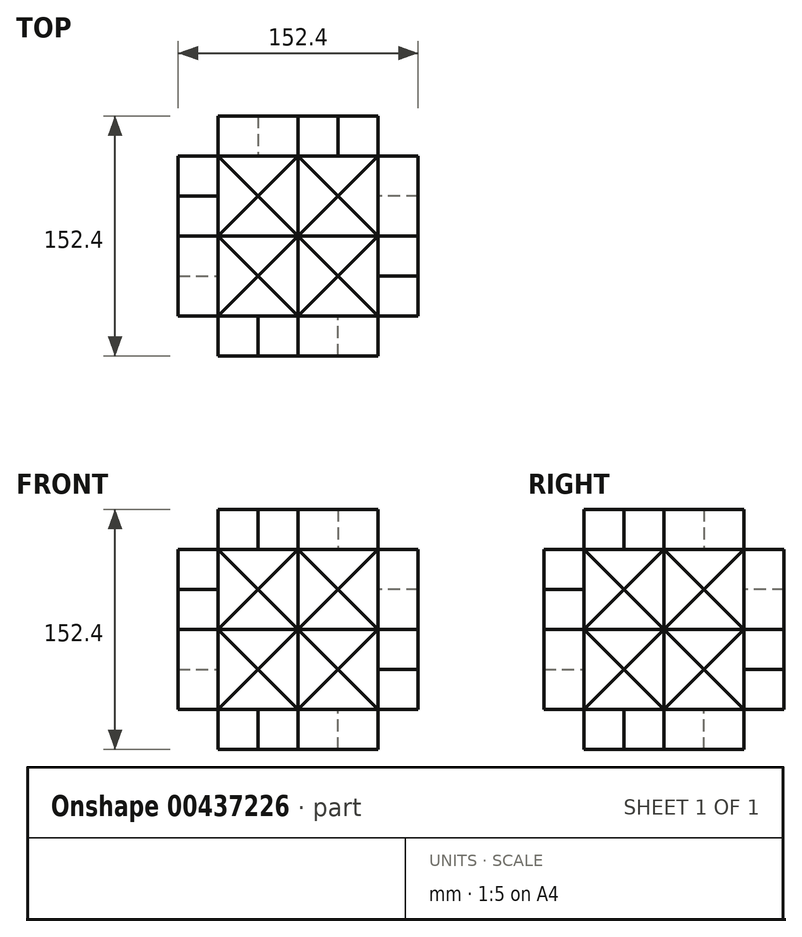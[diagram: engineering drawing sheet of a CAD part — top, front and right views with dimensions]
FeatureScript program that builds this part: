
annotation { "Feature Type Name" : "Feature", "Feature Type Description" : "" }
export const myFeature = defineFeature(function(context is Context, id is Id, definition is map)
    precondition{}
    {
        {
            var Q0;
            Q0=qCreatedBy(makeId("Front.planeOp"),FACE);
            var sketch = newSketch(context, id + "F0", { "sketchPlane" : qUnion([Q0])});
            skLineSegment(sketch, "E0.bottom", {"start": v(-48.5, 57.93) * mm, "end": v(53.1, 57.93) * mm});
            skLineSegment(sketch, "E0.top", {"start": v(-48.5, -43.67) * mm, "end": v(53.1, -43.67) * mm});
            skLineSegment(sketch, "E0.left", {"start": v(-48.5, 57.93) * mm, "end": v(-48.5, -43.67) * mm});
            skLineSegment(sketch, "E0.right", {"start": v(53.1, 57.93) * mm, "end": v(53.1, -43.67) * mm});
            skLineSegment(sketch, "E1", {"start": v(-48.5, 57.93) * mm, "end": v(53.1, -43.67) * mm});
            skLineSegment(sketch, "E2", {"start": v(53.1, 57.93) * mm, "end": v(-48.5, -43.67) * mm});
            skLineSegment(sketch, "E3", {"start": v(2.3, 7.13) * mm, "end": v(2.3, 57.93) * mm});
            skLineSegment(sketch, "E4", {"start": v(2.3, 7.13) * mm, "end": v(2.3, -43.67) * mm});
            skLineSegment(sketch, "E5", {"start": v(2.3, 7.13) * mm, "end": v(53.1, 7.13) * mm});
            skLineSegment(sketch, "E6", {"start": v(53.1, 7.13) * mm, "end": v(-48.5, 7.13) * mm});
            skLineSegment(sketch, "E7", {"start": v(2.3, 57.93) * mm, "end": v(-48.5, 7.13) * mm});
            skLineSegment(sketch, "E8", {"start": v(2.3, 57.93) * mm, "end": v(53.1, 7.13) * mm});
            skLineSegment(sketch, "E9", {"start": v(53.1, 7.13) * mm, "end": v(2.3, -43.67) * mm});
            skLineSegment(sketch, "E10", {"start": v(2.3, -43.67) * mm, "end": v(-48.5, 7.13) * mm});
            skSolve(sketch);
        }
        {
            var Q0;
            Q0 = qSketchRegion(id + "F0", true);
            extrude(context, id + "F1", {"entities" : qUnion([Q0]), "oppositeDirection" : true, "depth" : 101.6 * mm});
        }
        {
            var Q0;
            Q0=makeQuery(id+"F1.opExtrude","SWEPT_FACE",FACE,{"disambiguationData":[OSD([sQuery(id+"F0.wireOp",EDGE,"E0.right")])]});
            var sketch = newSketch(context, id + "F2", { "sketchPlane" : qUnion([Q0])});
            skLineSegment(sketch, "E11", {"start": v(0, 57.93) * mm, "end": v(101.6, -43.67) * mm});
            skLineSegment(sketch, "E12", {"start": v(101.6, -43.67) * mm, "end": v(101.6, 57.93) * mm});
            skLineSegment(sketch, "E13", {"start": v(101.6, 57.93) * mm, "end": v(0, -43.67) * mm});
            skLineSegment(sketch, "E14", {"start": v(50.8, -43.67) * mm, "end": v(50.8, 57.93) * mm});
            skLineSegment(sketch, "E15", {"start": v(50.8, 57.93) * mm, "end": v(0, 7.13) * mm});
            skLineSegment(sketch, "E16", {"start": v(0, 7.13) * mm, "end": v(101.6, 7.13) * mm});
            skLineSegment(sketch, "E17", {"start": v(101.6, 7.13) * mm, "end": v(50.8, 57.93) * mm});
            skLineSegment(sketch, "E18", {"start": v(0, 7.13) * mm, "end": v(50.8, -43.67) * mm});
            skLineSegment(sketch, "E19", {"start": v(101.6, 7.13) * mm, "end": v(50.8, -43.67) * mm});
            skSolve(sketch);
        }
        {
            var Q0;
            Q0=makeQuery(id+"F1.opExtrude","SWEPT_FACE",FACE,{"disambiguationData":[OSD([sQuery(id+"F0.wireOp",EDGE,"E0.bottom")])]});
            var sketch = newSketch(context, id + "F3", { "sketchPlane" : qUnion([Q0])});
            skLineSegment(sketch, "E20", {"start": v(-48.5, 0) * mm, "end": v(53.1, 101.6) * mm});
            skLineSegment(sketch, "E21", {"start": v(53.1, 101.6) * mm, "end": v(-48.5, 101.6) * mm});
            skLineSegment(sketch, "E22", {"start": v(-48.5, 101.6) * mm, "end": v(53.1, 0) * mm});
            skLineSegment(sketch, "E23", {"start": v(2.3, 0) * mm, "end": v(2.3, 101.6) * mm});
            skLineSegment(sketch, "E24", {"start": v(2.3, 101.6) * mm, "end": v(-48.5, 50.8) * mm});
            skLineSegment(sketch, "E25", {"start": v(-48.5, 50.8) * mm, "end": v(53.1, 50.8) * mm});
            skLineSegment(sketch, "E26", {"start": v(53.1, 50.8) * mm, "end": v(2.3, 101.6) * mm});
            skLineSegment(sketch, "E27", {"start": v(-48.5, 50.8) * mm, "end": v(2.3, 0) * mm});
            skLineSegment(sketch, "E28", {"start": v(53.1, 50.8) * mm, "end": v(2.3, 0) * mm});
            skSolve(sketch);
        }
        {
            var Q0;
            Q0=makeQuery(id+"F1.opExtrude","SWEPT_FACE",FACE,{"disambiguationData":[OSD([sQuery(id+"F0.wireOp",EDGE,"E0.left")])]});
            var sketch = newSketch(context, id + "F4", { "sketchPlane" : qUnion([Q0])});
            skLineSegment(sketch, "E29", {"start": v(-101.6, 57.93) * mm, "end": v(0, -43.67) * mm});
            skLineSegment(sketch, "E30", {"start": v(0, -43.67) * mm, "end": v(0, 57.93) * mm});
            skLineSegment(sketch, "E31", {"start": v(0, 57.93) * mm, "end": v(-101.6, -43.67) * mm});
            skLineSegment(sketch, "E32", {"start": v(-50.8, -43.67) * mm, "end": v(-50.8, 57.93) * mm});
            skLineSegment(sketch, "E33", {"start": v(-50.8, 57.93) * mm, "end": v(-101.6, 7.13) * mm});
            skLineSegment(sketch, "E34", {"start": v(-101.6, 7.13) * mm, "end": v(0, 7.13) * mm});
            skLineSegment(sketch, "E35", {"start": v(0, 7.13) * mm, "end": v(-50.8, 57.93) * mm});
            skLineSegment(sketch, "E36", {"start": v(-101.6, 7.13) * mm, "end": v(-50.8, -43.67) * mm});
            skLineSegment(sketch, "E37", {"start": v(0, 7.13) * mm, "end": v(-50.8, -43.67) * mm});
            skSolve(sketch);
        }
        {
            var Q0;
            Q0=makeQuery(id+"F1.opExtrude","CAP_FACE",FACE,{"disambiguationData":[OSD([sQuery(id+"F0.wireOp",EDGE,"E0.bottom"),sQuery(id+"F0.wireOp",EDGE,"E0.top"),sQuery(id+"F0.wireOp",EDGE,"E0.left"),sQuery(id+"F0.wireOp",EDGE,"E0.right")])],"isStart":false});
            var sketch = newSketch(context, id + "F5", { "sketchPlane" : qUnion([Q0])});
            skLineSegment(sketch, "E38", {"start": v(-53.1, 57.93) * mm, "end": v(48.5, -43.67) * mm});
            skLineSegment(sketch, "E39", {"start": v(48.5, -43.67) * mm, "end": v(48.5, 57.93) * mm});
            skLineSegment(sketch, "E40", {"start": v(-53.1, -43.67) * mm, "end": v(48.5, 57.93) * mm});
            skLineSegment(sketch, "E41", {"start": v(-2.3, 57.93) * mm, "end": v(-2.3, -43.67) * mm});
            skLineSegment(sketch, "E42", {"start": v(-2.3, -43.67) * mm, "end": v(-53.1, 7.13) * mm});
            skLineSegment(sketch, "E43", {"start": v(-53.1, 7.13) * mm, "end": v(48.5, 7.13) * mm});
            skLineSegment(sketch, "E44", {"start": v(48.5, 7.13) * mm, "end": v(-2.3, 57.93) * mm});
            skLineSegment(sketch, "E45", {"start": v(-53.1, 7.13) * mm, "end": v(-2.3, 57.93) * mm});
            skLineSegment(sketch, "E46", {"start": v(-2.3, -43.67) * mm, "end": v(48.5, 7.13) * mm});
            skSolve(sketch);
        }
        {
            var Q0;
            Q0=makeQuery(id+"F1.opExtrude","SWEPT_FACE",FACE,{"disambiguationData":[OSD([sQuery(id+"F0.wireOp",EDGE,"E0.top")])]});
            var sketch = newSketch(context, id + "F6", { "sketchPlane" : qUnion([Q0])});
            skLineSegment(sketch, "E47", {"start": v(-48.5, 0) * mm, "end": v(53.1, -101.6) * mm});
            skLineSegment(sketch, "E48", {"start": v(53.1, -101.6) * mm, "end": v(53.1, 0) * mm});
            skLineSegment(sketch, "E49", {"start": v(53.1, 0) * mm, "end": v(-48.5, -101.6) * mm});
            skLineSegment(sketch, "E50", {"start": v(2.3, -101.6) * mm, "end": v(2.3, 0) * mm});
            skLineSegment(sketch, "E51", {"start": v(2.3, 0) * mm, "end": v(-48.5, -50.8) * mm});
            skLineSegment(sketch, "E52", {"start": v(-48.5, -50.8) * mm, "end": v(53.1, -50.8) * mm});
            skLineSegment(sketch, "E53", {"start": v(53.1, -50.8) * mm, "end": v(2.3, 0) * mm});
            skLineSegment(sketch, "E54", {"start": v(-48.5, -50.8) * mm, "end": v(2.3, -101.6) * mm});
            skLineSegment(sketch, "E55", {"start": v(53.1, -50.8) * mm, "end": v(2.3, -101.6) * mm});
            skSolve(sketch);
        }
        {
            var Q0;
            {var subQ0=sQuery(id+"F0.wireOp",EDGE,"E1");var subQ3=sQuery(id+"F0.wireOp",EDGE,"E7");var subQ5=makeQuery(id+"F0.imprint","INTERSECT",VERTEX,{"derivedFrom":[subQ0,subQ3]});Q0=makeQuery(id+"F0.imprint","IMPRINT",FACE,{"disambiguationData":[TD([[makeQuery(id+"F0.imprint","IMPRINT",EDGE,{"disambiguationData":[TD([[subQ5,1.0]])],"derivedFrom":subQ0}),-1.0]])]});}
            var Q1;
            {var subQ0=sQuery(id+"F0.wireOp",EDGE,"E3");Q1=makeQuery(id+"F0.imprint","IMPRINT",FACE,{"disambiguationData":[TD([[makeQuery(id+"F0.imprint","IMPRINT",EDGE,{"derivedFrom":subQ0}),1.0]])]});}
            var Q2;
            {var subQ0=sQuery(id+"F0.wireOp",EDGE,"E2");var subQ3=sQuery(id+"F0.wireOp",EDGE,"E8");var subQ5=makeQuery(id+"F0.imprint","INTERSECT",VERTEX,{"derivedFrom":[subQ0,subQ3]});Q2=makeQuery(id+"F0.imprint","IMPRINT",FACE,{"disambiguationData":[TD([[makeQuery(id+"F0.imprint","IMPRINT",EDGE,{"disambiguationData":[TD([[subQ5,1.0]])],"derivedFrom":subQ0}),-1.0]])]});}
            var Q3;
            {var subQ1=sQuery(id+"F0.wireOp",EDGE,"E2");var subQ3=sQuery(id+"F0.wireOp",EDGE,"E8");var subQ4=makeQuery(id+"F0.imprint","INTERSECT",VERTEX,{"derivedFrom":[subQ1,subQ3]});Q3=makeQuery(id+"F0.imprint","IMPRINT",FACE,{"disambiguationData":[TD([[makeQuery(id+"F0.imprint","IMPRINT",EDGE,{"disambiguationData":[TD([[subQ4,-1.0]])],"derivedFrom":subQ3}),-1.0]])]});}
            var Q4;
            {var subQ0=sQuery(id+"F0.wireOp",EDGE,"E4");Q4=makeQuery(id+"F0.imprint","IMPRINT",FACE,{"disambiguationData":[TD([[makeQuery(id+"F0.imprint","IMPRINT",EDGE,{"derivedFrom":subQ0}),1.0]])]});}
            var Q5;
            {var subQ0=sQuery(id+"F0.wireOp",EDGE,"E1");var subQ3=sQuery(id+"F0.wireOp",EDGE,"E9");var subQ5=makeQuery(id+"F0.imprint","INTERSECT",VERTEX,{"derivedFrom":[subQ0,subQ3]});Q5=makeQuery(id+"F0.imprint","IMPRINT",FACE,{"disambiguationData":[TD([[makeQuery(id+"F0.imprint","IMPRINT",EDGE,{"disambiguationData":[TD([[subQ5,-1.0]])],"derivedFrom":subQ0}),1.0]])]});}
            var Q6;
            {var subQ1=sQuery(id+"F0.wireOp",EDGE,"E2");var subQ3=sQuery(id+"F0.wireOp",EDGE,"E10");var subQ4=makeQuery(id+"F0.imprint","INTERSECT",VERTEX,{"derivedFrom":[subQ1,subQ3]});Q6=makeQuery(id+"F0.imprint","IMPRINT",FACE,{"disambiguationData":[TD([[makeQuery(id+"F0.imprint","IMPRINT",EDGE,{"disambiguationData":[TD([[subQ4,-1.0]])],"derivedFrom":subQ3}),-1.0]])]});}
            var Q7;
            {var subQ0=sQuery(id+"F0.wireOp",EDGE,"E2");var subQ3=sQuery(id+"F0.wireOp",EDGE,"E10");var subQ5=makeQuery(id+"F0.imprint","INTERSECT",VERTEX,{"derivedFrom":[subQ0,subQ3]});Q7=makeQuery(id+"F0.imprint","IMPRINT",FACE,{"disambiguationData":[TD([[makeQuery(id+"F0.imprint","IMPRINT",EDGE,{"disambiguationData":[TD([[subQ5,-1.0]])],"derivedFrom":subQ0}),1.0]])]});}
            extrude(context, id + "F7", {"entities" : qUnion([Q0, Q1, Q2, Q3, Q4, Q5, Q6, Q7]), "depth" : 25.4 * mm});
        }
        {
            var Q0;
            {var subQ0=sQuery(id+"F2.wireOp",EDGE,"E11");var subQ4=sQuery(id+"F2.wireOp",EDGE,"E15");var subQ5=makeQuery(id+"F2.imprint","INTERSECT",VERTEX,{"derivedFrom":[subQ0,subQ4]});Q0=makeQuery(id+"F2.imprint","IMPRINT",FACE,{"disambiguationData":[TD([[makeQuery(id+"F2.imprint","IMPRINT",EDGE,{"disambiguationData":[TD([[subQ5,-1.0]])],"derivedFrom":subQ4}),-1.0]])]});}
            var Q1;
            {var subQ0=sQuery(id+"F2.wireOp",EDGE,"E15");var subQ1=sQuery(id+"F2.wireOp",EDGE,"E11");var subQ2=makeQuery(id+"F2.imprint","INTERSECT",VERTEX,{"derivedFrom":[subQ1,subQ0]});Q1=makeQuery(id+"F2.imprint","IMPRINT",FACE,{"disambiguationData":[TD([[makeQuery(id+"F2.imprint","IMPRINT",EDGE,{"disambiguationData":[TD([[subQ2,-1.0]])],"derivedFrom":subQ1}),1.0]])]});}
            var Q2;
            {var subQ0=sQuery(id+"F2.wireOp",EDGE,"E13");var subQ3=sQuery(id+"F2.wireOp",EDGE,"E17");var subQ4=makeQuery(id+"F2.imprint","INTERSECT",VERTEX,{"derivedFrom":[subQ0,subQ3]});Q2=makeQuery(id+"F2.imprint","IMPRINT",FACE,{"disambiguationData":[TD([[makeQuery(id+"F2.imprint","IMPRINT",EDGE,{"disambiguationData":[TD([[subQ4,1.0]])],"derivedFrom":subQ0}),-1.0]])]});}
            var Q3;
            {var subQ0=sQuery(id+"F2.wireOp",EDGE,"E17");var subQ1=sQuery(id+"F2.wireOp",EDGE,"E13");var subQ2=makeQuery(id+"F2.imprint","INTERSECT",VERTEX,{"derivedFrom":[subQ1,subQ0]});Q3=makeQuery(id+"F2.imprint","IMPRINT",FACE,{"disambiguationData":[TD([[makeQuery(id+"F2.imprint","IMPRINT",EDGE,{"disambiguationData":[TD([[subQ2,-1.0]])],"derivedFrom":subQ1}),1.0]])]});}
            var Q4;
            {var subQ1=sQuery(id+"F2.wireOp",EDGE,"E11");var subQ3=sQuery(id+"F2.wireOp",EDGE,"E19");var subQ4=makeQuery(id+"F2.imprint","INTERSECT",VERTEX,{"derivedFrom":[subQ1,subQ3]});Q4=makeQuery(id+"F2.imprint","IMPRINT",FACE,{"disambiguationData":[TD([[makeQuery(id+"F2.imprint","IMPRINT",EDGE,{"disambiguationData":[TD([[subQ4,1.0]])],"derivedFrom":subQ3}),1.0]])]});}
            var Q5;
            {var subQ0=sQuery(id+"F2.wireOp",EDGE,"E19");var subQ1=sQuery(id+"F2.wireOp",EDGE,"E11");var subQ2=makeQuery(id+"F2.imprint","INTERSECT",VERTEX,{"derivedFrom":[subQ1,subQ0]});Q5=makeQuery(id+"F2.imprint","IMPRINT",FACE,{"disambiguationData":[TD([[makeQuery(id+"F2.imprint","IMPRINT",EDGE,{"disambiguationData":[TD([[subQ2,1.0]])],"derivedFrom":subQ1}),-1.0]])]});}
            var Q6;
            {var subQ0=sQuery(id+"F2.wireOp",EDGE,"E18");var subQ1=sQuery(id+"F2.wireOp",EDGE,"E13");var subQ2=makeQuery(id+"F2.imprint","INTERSECT",VERTEX,{"derivedFrom":[subQ1,subQ0]});Q6=makeQuery(id+"F2.imprint","IMPRINT",FACE,{"disambiguationData":[TD([[makeQuery(id+"F2.imprint","IMPRINT",EDGE,{"disambiguationData":[TD([[subQ2,1.0]])],"derivedFrom":subQ1}),-1.0]])]});}
            var Q7;
            {var subQ0=sQuery(id+"F2.wireOp",EDGE,"E13");var subQ4=sQuery(id+"F2.wireOp",EDGE,"E18");var subQ5=makeQuery(id+"F2.imprint","INTERSECT",VERTEX,{"derivedFrom":[subQ0,subQ4]});Q7=makeQuery(id+"F2.imprint","IMPRINT",FACE,{"disambiguationData":[TD([[makeQuery(id+"F2.imprint","IMPRINT",EDGE,{"disambiguationData":[TD([[subQ5,-1.0]])],"derivedFrom":subQ0}),1.0]])]});}
            extrude(context, id + "F8", {"entities" : qUnion([Q0, Q1, Q2, Q3, Q4, Q5, Q6, Q7]), "depth" : 25.4 * mm});
        }
        {
            var Q0;
            {var subQ0=sQuery(id+"F4.wireOp",EDGE,"E31");var subQ3=sQuery(id+"F4.wireOp",EDGE,"E35");var subQ4=makeQuery(id+"F4.imprint","INTERSECT",VERTEX,{"derivedFrom":[subQ0,subQ3]});Q0=makeQuery(id+"F4.imprint","IMPRINT",FACE,{"disambiguationData":[TD([[makeQuery(id+"F4.imprint","IMPRINT",EDGE,{"disambiguationData":[TD([[subQ4,1.0]])],"derivedFrom":subQ0}),-1.0]])]});}
            var Q1;
            {var subQ0=sQuery(id+"F4.wireOp",EDGE,"E35");var subQ1=sQuery(id+"F4.wireOp",EDGE,"E31");var subQ2=makeQuery(id+"F4.imprint","INTERSECT",VERTEX,{"derivedFrom":[subQ1,subQ0]});Q1=makeQuery(id+"F4.imprint","IMPRINT",FACE,{"disambiguationData":[TD([[makeQuery(id+"F4.imprint","IMPRINT",EDGE,{"disambiguationData":[TD([[subQ2,-1.0]])],"derivedFrom":subQ1}),1.0]])]});}
            var Q2;
            {var subQ0=sQuery(id+"F4.wireOp",EDGE,"E37");var subQ1=sQuery(id+"F4.wireOp",EDGE,"E29");var subQ2=makeQuery(id+"F4.imprint","INTERSECT",VERTEX,{"derivedFrom":[subQ1,subQ0]});Q2=makeQuery(id+"F4.imprint","IMPRINT",FACE,{"disambiguationData":[TD([[makeQuery(id+"F4.imprint","IMPRINT",EDGE,{"disambiguationData":[TD([[subQ2,1.0]])],"derivedFrom":subQ1}),-1.0]])]});}
            var Q3;
            {var subQ1=sQuery(id+"F4.wireOp",EDGE,"E29");var subQ3=sQuery(id+"F4.wireOp",EDGE,"E37");var subQ4=makeQuery(id+"F4.imprint","INTERSECT",VERTEX,{"derivedFrom":[subQ1,subQ3]});Q3=makeQuery(id+"F4.imprint","IMPRINT",FACE,{"disambiguationData":[TD([[makeQuery(id+"F4.imprint","IMPRINT",EDGE,{"disambiguationData":[TD([[subQ4,1.0]])],"derivedFrom":subQ3}),1.0]])]});}
            var Q4;
            {var subQ0=sQuery(id+"F4.wireOp",EDGE,"E36");var subQ1=sQuery(id+"F4.wireOp",EDGE,"E31");var subQ2=makeQuery(id+"F4.imprint","INTERSECT",VERTEX,{"derivedFrom":[subQ1,subQ0]});Q4=makeQuery(id+"F4.imprint","IMPRINT",FACE,{"disambiguationData":[TD([[makeQuery(id+"F4.imprint","IMPRINT",EDGE,{"disambiguationData":[TD([[subQ2,1.0]])],"derivedFrom":subQ1}),-1.0]])]});}
            var Q5;
            {var subQ0=sQuery(id+"F4.wireOp",EDGE,"E31");var subQ4=sQuery(id+"F4.wireOp",EDGE,"E36");var subQ5=makeQuery(id+"F4.imprint","INTERSECT",VERTEX,{"derivedFrom":[subQ0,subQ4]});Q5=makeQuery(id+"F4.imprint","IMPRINT",FACE,{"disambiguationData":[TD([[makeQuery(id+"F4.imprint","IMPRINT",EDGE,{"disambiguationData":[TD([[subQ5,-1.0]])],"derivedFrom":subQ0}),1.0]])]});}
            var Q6;
            {var subQ0=sQuery(id+"F4.wireOp",EDGE,"E29");var subQ4=sQuery(id+"F4.wireOp",EDGE,"E33");var subQ5=makeQuery(id+"F4.imprint","INTERSECT",VERTEX,{"derivedFrom":[subQ0,subQ4]});Q6=makeQuery(id+"F4.imprint","IMPRINT",FACE,{"disambiguationData":[TD([[makeQuery(id+"F4.imprint","IMPRINT",EDGE,{"disambiguationData":[TD([[subQ5,-1.0]])],"derivedFrom":subQ4}),-1.0]])]});}
            var Q7;
            {var subQ0=sQuery(id+"F4.wireOp",EDGE,"E33");var subQ1=sQuery(id+"F4.wireOp",EDGE,"E29");var subQ2=makeQuery(id+"F4.imprint","INTERSECT",VERTEX,{"derivedFrom":[subQ1,subQ0]});Q7=makeQuery(id+"F4.imprint","IMPRINT",FACE,{"disambiguationData":[TD([[makeQuery(id+"F4.imprint","IMPRINT",EDGE,{"disambiguationData":[TD([[subQ2,-1.0]])],"derivedFrom":subQ1}),1.0]])]});}
            extrude(context, id + "F9", {"entities" : qUnion([Q0, Q1, Q2, Q3, Q4, Q5, Q6, Q7]), "depth" : 25.4 * mm});
        }
        {
            var Q0;
            {var subQ0=sQuery(id+"F5.wireOp",EDGE,"E40");var subQ3=sQuery(id+"F5.wireOp",EDGE,"E44");var subQ4=makeQuery(id+"F5.imprint","INTERSECT",VERTEX,{"derivedFrom":[subQ0,subQ3]});Q0=makeQuery(id+"F5.imprint","IMPRINT",FACE,{"disambiguationData":[TD([[makeQuery(id+"F5.imprint","IMPRINT",EDGE,{"disambiguationData":[TD([[subQ4,-1.0]])],"derivedFrom":subQ0}),1.0]])]});}
            var Q1;
            {var subQ0=sQuery(id+"F5.wireOp",EDGE,"E44");var subQ1=sQuery(id+"F5.wireOp",EDGE,"E40");var subQ2=makeQuery(id+"F5.imprint","INTERSECT",VERTEX,{"derivedFrom":[subQ1,subQ0]});Q1=makeQuery(id+"F5.imprint","IMPRINT",FACE,{"disambiguationData":[TD([[makeQuery(id+"F5.imprint","IMPRINT",EDGE,{"disambiguationData":[TD([[subQ2,1.0]])],"derivedFrom":subQ1}),-1.0]])]});}
            var Q2;
            {var subQ0=sQuery(id+"F5.wireOp",EDGE,"E46");var subQ1=sQuery(id+"F5.wireOp",EDGE,"E38");var subQ2=makeQuery(id+"F5.imprint","INTERSECT",VERTEX,{"derivedFrom":[subQ1,subQ0]});Q2=makeQuery(id+"F5.imprint","IMPRINT",FACE,{"disambiguationData":[TD([[makeQuery(id+"F5.imprint","IMPRINT",EDGE,{"disambiguationData":[TD([[subQ2,1.0]])],"derivedFrom":subQ1}),-1.0]])]});}
            var Q3;
            {var subQ1=sQuery(id+"F5.wireOp",EDGE,"E38");var subQ3=sQuery(id+"F5.wireOp",EDGE,"E46");var subQ4=makeQuery(id+"F5.imprint","INTERSECT",VERTEX,{"derivedFrom":[subQ1,subQ3]});Q3=makeQuery(id+"F5.imprint","IMPRINT",FACE,{"disambiguationData":[TD([[makeQuery(id+"F5.imprint","IMPRINT",EDGE,{"disambiguationData":[TD([[subQ4,-1.0]])],"derivedFrom":subQ1}),1.0]])]});}
            var Q4;
            {var subQ0=sQuery(id+"F5.wireOp",EDGE,"E42");var subQ1=sQuery(id+"F5.wireOp",EDGE,"E40");var subQ2=makeQuery(id+"F5.imprint","INTERSECT",VERTEX,{"derivedFrom":[subQ1,subQ0]});Q4=makeQuery(id+"F5.imprint","IMPRINT",FACE,{"disambiguationData":[TD([[makeQuery(id+"F5.imprint","IMPRINT",EDGE,{"disambiguationData":[TD([[subQ2,-1.0]])],"derivedFrom":subQ1}),1.0]])]});}
            var Q5;
            {var subQ0=sQuery(id+"F5.wireOp",EDGE,"E40");var subQ3=sQuery(id+"F5.wireOp",EDGE,"E42");var subQ4=makeQuery(id+"F5.imprint","INTERSECT",VERTEX,{"derivedFrom":[subQ0,subQ3]});Q5=makeQuery(id+"F5.imprint","IMPRINT",FACE,{"disambiguationData":[TD([[makeQuery(id+"F5.imprint","IMPRINT",EDGE,{"disambiguationData":[TD([[subQ4,1.0]])],"derivedFrom":subQ0}),-1.0]])]});}
            var Q6;
            {var subQ0=sQuery(id+"F5.wireOp",EDGE,"E38");var subQ3=sQuery(id+"F5.wireOp",EDGE,"E45");var subQ4=makeQuery(id+"F5.imprint","INTERSECT",VERTEX,{"derivedFrom":[subQ0,subQ3]});Q6=makeQuery(id+"F5.imprint","IMPRINT",FACE,{"disambiguationData":[TD([[makeQuery(id+"F5.imprint","IMPRINT",EDGE,{"disambiguationData":[TD([[subQ4,1.0]])],"derivedFrom":subQ0}),-1.0]])]});}
            var Q7;
            {var subQ0=sQuery(id+"F5.wireOp",EDGE,"E45");var subQ1=sQuery(id+"F5.wireOp",EDGE,"E38");var subQ2=makeQuery(id+"F5.imprint","INTERSECT",VERTEX,{"derivedFrom":[subQ1,subQ0]});Q7=makeQuery(id+"F5.imprint","IMPRINT",FACE,{"disambiguationData":[TD([[makeQuery(id+"F5.imprint","IMPRINT",EDGE,{"disambiguationData":[TD([[subQ2,-1.0]])],"derivedFrom":subQ1}),1.0]])]});}
            extrude(context, id + "F10", {"entities" : qUnion([Q0, Q1, Q2, Q3, Q4, Q5, Q6, Q7]), "depth" : 25.4 * mm});
        }
        {
            var Q0;
            {var subQ0=sQuery(id+"F3.wireOp",EDGE,"E20");var subQ4=sQuery(id+"F3.wireOp",EDGE,"E27");var subQ5=makeQuery(id+"F3.imprint","INTERSECT",VERTEX,{"derivedFrom":[subQ0,subQ4]});Q0=makeQuery(id+"F3.imprint","IMPRINT",FACE,{"disambiguationData":[TD([[makeQuery(id+"F3.imprint","IMPRINT",EDGE,{"disambiguationData":[TD([[subQ5,1.0]])],"derivedFrom":subQ0}),1.0]])]});}
            var Q1;
            {var subQ0=sQuery(id+"F3.wireOp",EDGE,"E27");var subQ1=sQuery(id+"F3.wireOp",EDGE,"E20");var subQ2=makeQuery(id+"F3.imprint","INTERSECT",VERTEX,{"derivedFrom":[subQ1,subQ0]});Q1=makeQuery(id+"F3.imprint","IMPRINT",FACE,{"disambiguationData":[TD([[makeQuery(id+"F3.imprint","IMPRINT",EDGE,{"disambiguationData":[TD([[subQ2,-1.0]])],"derivedFrom":subQ1}),-1.0]])]});}
            var Q2;
            {var subQ0=sQuery(id+"F3.wireOp",EDGE,"E28");var subQ1=sQuery(id+"F3.wireOp",EDGE,"E22");var subQ2=makeQuery(id+"F3.imprint","INTERSECT",VERTEX,{"derivedFrom":[subQ1,subQ0]});Q2=makeQuery(id+"F3.imprint","IMPRINT",FACE,{"disambiguationData":[TD([[makeQuery(id+"F3.imprint","IMPRINT",EDGE,{"disambiguationData":[TD([[subQ2,1.0]])],"derivedFrom":subQ1}),1.0]])]});}
            var Q3;
            {var subQ0=sQuery(id+"F3.wireOp",EDGE,"E22");var subQ4=sQuery(id+"F3.wireOp",EDGE,"E28");var subQ5=makeQuery(id+"F3.imprint","INTERSECT",VERTEX,{"derivedFrom":[subQ0,subQ4]});Q3=makeQuery(id+"F3.imprint","IMPRINT",FACE,{"disambiguationData":[TD([[makeQuery(id+"F3.imprint","IMPRINT",EDGE,{"disambiguationData":[TD([[subQ5,-1.0]])],"derivedFrom":subQ4}),1.0]])]});}
            var Q4;
            {var subQ0=sQuery(id+"F3.wireOp",EDGE,"E26");var subQ1=sQuery(id+"F3.wireOp",EDGE,"E20");var subQ2=makeQuery(id+"F3.imprint","INTERSECT",VERTEX,{"derivedFrom":[subQ1,subQ0]});Q4=makeQuery(id+"F3.imprint","IMPRINT",FACE,{"disambiguationData":[TD([[makeQuery(id+"F3.imprint","IMPRINT",EDGE,{"disambiguationData":[TD([[subQ2,1.0]])],"derivedFrom":subQ1}),1.0]])]});}
            var Q5;
            {var subQ0=sQuery(id+"F3.wireOp",EDGE,"E20");var subQ3=sQuery(id+"F3.wireOp",EDGE,"E26");var subQ4=makeQuery(id+"F3.imprint","INTERSECT",VERTEX,{"derivedFrom":[subQ0,subQ3]});Q5=makeQuery(id+"F3.imprint","IMPRINT",FACE,{"disambiguationData":[TD([[makeQuery(id+"F3.imprint","IMPRINT",EDGE,{"disambiguationData":[TD([[subQ4,-1.0]])],"derivedFrom":subQ0}),-1.0]])]});}
            var Q6;
            {var subQ0=sQuery(id+"F3.wireOp",EDGE,"E22");var subQ3=sQuery(id+"F3.wireOp",EDGE,"E24");var subQ5=makeQuery(id+"F3.imprint","INTERSECT",VERTEX,{"derivedFrom":[subQ0,subQ3]});Q6=makeQuery(id+"F3.imprint","IMPRINT",FACE,{"disambiguationData":[TD([[makeQuery(id+"F3.imprint","IMPRINT",EDGE,{"disambiguationData":[TD([[subQ5,1.0]])],"derivedFrom":subQ3}),-1.0]])]});}
            var Q7;
            {var subQ0=sQuery(id+"F3.wireOp",EDGE,"E24");var subQ1=sQuery(id+"F3.wireOp",EDGE,"E22");var subQ2=makeQuery(id+"F3.imprint","INTERSECT",VERTEX,{"derivedFrom":[subQ1,subQ0]});Q7=makeQuery(id+"F3.imprint","IMPRINT",FACE,{"disambiguationData":[TD([[makeQuery(id+"F3.imprint","IMPRINT",EDGE,{"disambiguationData":[TD([[subQ2,-1.0]])],"derivedFrom":subQ1}),-1.0]])]});}
            extrude(context, id + "F11", {"entities" : qUnion([Q0, Q1, Q2, Q3, Q4, Q5, Q6, Q7]), "depth" : 25.4 * mm});
        }
        {
            var Q0;
            {var subQ0=sQuery(id+"F6.wireOp",EDGE,"E47");var subQ4=sQuery(id+"F6.wireOp",EDGE,"E51");var subQ5=makeQuery(id+"F6.imprint","INTERSECT",VERTEX,{"derivedFrom":[subQ0,subQ4]});Q0=makeQuery(id+"F6.imprint","IMPRINT",FACE,{"disambiguationData":[TD([[makeQuery(id+"F6.imprint","IMPRINT",EDGE,{"disambiguationData":[TD([[subQ5,1.0]])],"derivedFrom":subQ0}),-1.0]])]});}
            var Q1;
            {var subQ0=sQuery(id+"F6.wireOp",EDGE,"E51");var subQ1=sQuery(id+"F6.wireOp",EDGE,"E47");var subQ2=makeQuery(id+"F6.imprint","INTERSECT",VERTEX,{"derivedFrom":[subQ1,subQ0]});Q1=makeQuery(id+"F6.imprint","IMPRINT",FACE,{"disambiguationData":[TD([[makeQuery(id+"F6.imprint","IMPRINT",EDGE,{"disambiguationData":[TD([[subQ2,-1.0]])],"derivedFrom":subQ1}),1.0]])]});}
            var Q2;
            {var subQ0=sQuery(id+"F6.wireOp",EDGE,"E49");var subQ3=sQuery(id+"F6.wireOp",EDGE,"E53");var subQ4=makeQuery(id+"F6.imprint","INTERSECT",VERTEX,{"derivedFrom":[subQ0,subQ3]});Q2=makeQuery(id+"F6.imprint","IMPRINT",FACE,{"disambiguationData":[TD([[makeQuery(id+"F6.imprint","IMPRINT",EDGE,{"disambiguationData":[TD([[subQ4,1.0]])],"derivedFrom":subQ0}),-1.0]])]});}
            var Q3;
            {var subQ0=sQuery(id+"F6.wireOp",EDGE,"E53");var subQ1=sQuery(id+"F6.wireOp",EDGE,"E49");var subQ2=makeQuery(id+"F6.imprint","INTERSECT",VERTEX,{"derivedFrom":[subQ1,subQ0]});Q3=makeQuery(id+"F6.imprint","IMPRINT",FACE,{"disambiguationData":[TD([[makeQuery(id+"F6.imprint","IMPRINT",EDGE,{"disambiguationData":[TD([[subQ2,-1.0]])],"derivedFrom":subQ1}),1.0]])]});}
            var Q4;
            {var subQ0=sQuery(id+"F6.wireOp",EDGE,"E55");var subQ1=sQuery(id+"F6.wireOp",EDGE,"E47");var subQ2=makeQuery(id+"F6.imprint","INTERSECT",VERTEX,{"derivedFrom":[subQ1,subQ0]});Q4=makeQuery(id+"F6.imprint","IMPRINT",FACE,{"disambiguationData":[TD([[makeQuery(id+"F6.imprint","IMPRINT",EDGE,{"disambiguationData":[TD([[subQ2,1.0]])],"derivedFrom":subQ1}),-1.0]])]});}
            var Q5;
            {var subQ1=sQuery(id+"F6.wireOp",EDGE,"E47");var subQ3=sQuery(id+"F6.wireOp",EDGE,"E55");var subQ4=makeQuery(id+"F6.imprint","INTERSECT",VERTEX,{"derivedFrom":[subQ1,subQ3]});Q5=makeQuery(id+"F6.imprint","IMPRINT",FACE,{"disambiguationData":[TD([[makeQuery(id+"F6.imprint","IMPRINT",EDGE,{"disambiguationData":[TD([[subQ4,-1.0]])],"derivedFrom":subQ1}),1.0]])]});}
            var Q6;
            {var subQ0=sQuery(id+"F6.wireOp",EDGE,"E54");var subQ1=sQuery(id+"F6.wireOp",EDGE,"E49");var subQ2=makeQuery(id+"F6.imprint","INTERSECT",VERTEX,{"derivedFrom":[subQ1,subQ0]});Q6=makeQuery(id+"F6.imprint","IMPRINT",FACE,{"disambiguationData":[TD([[makeQuery(id+"F6.imprint","IMPRINT",EDGE,{"disambiguationData":[TD([[subQ2,1.0]])],"derivedFrom":subQ1}),-1.0]])]});}
            var Q7;
            {var subQ0=sQuery(id+"F6.wireOp",EDGE,"E49");var subQ4=sQuery(id+"F6.wireOp",EDGE,"E54");var subQ5=makeQuery(id+"F6.imprint","INTERSECT",VERTEX,{"derivedFrom":[subQ0,subQ4]});Q7=makeQuery(id+"F6.imprint","IMPRINT",FACE,{"disambiguationData":[TD([[makeQuery(id+"F6.imprint","IMPRINT",EDGE,{"disambiguationData":[TD([[subQ5,-1.0]])],"derivedFrom":subQ4}),-1.0]])]});}
            extrude(context, id + "F12", {"entities" : qUnion([Q0, Q1, Q2, Q3, Q4, Q5, Q6, Q7]), "depth" : 25.4 * mm});
        }
    });
